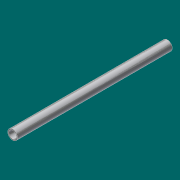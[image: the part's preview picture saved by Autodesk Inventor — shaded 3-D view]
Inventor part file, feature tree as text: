
AUTODESK INVENTOR PART (.ipt)
format: ipt  version: 2017 (Build 210142000, 142)  size: 105,472 bytes
history: native  units: in
note: dims shown in document units (in); Inventor stores cm internally (conversion verified against a paired STEP export)
features: extrude x1, sketch x1
ambient origin geometry x8: Origin, YZ Plane, XZ Plane, XY Plane, X Axis, Y Axis, Z Axis, Center Point
bodies: Solid1 (feature_tree)
feature tree (2):
  extrude  "Extrusion1"  Depth=30.25in
  sketch  "Sketch1"  dims[d0=1.9in d1=1.5in d2=30.25in d3=0.0in]
